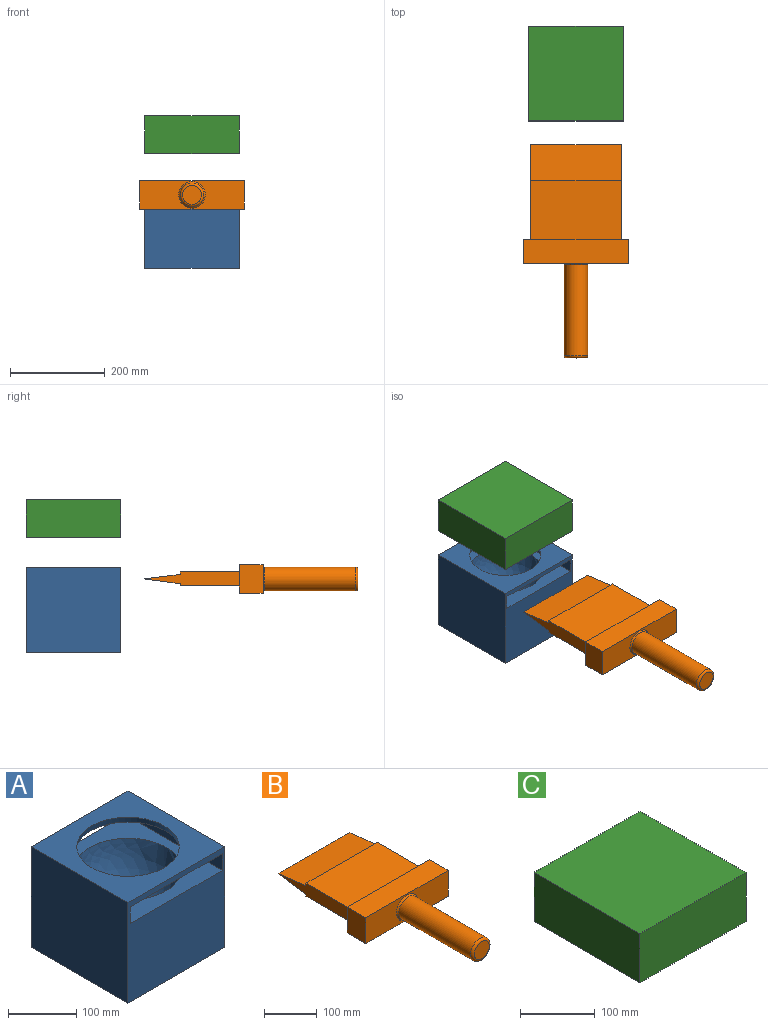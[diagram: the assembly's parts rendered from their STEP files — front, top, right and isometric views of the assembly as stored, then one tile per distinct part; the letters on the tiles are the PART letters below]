
ASSEMBLY  parts=3 mates=2
PART A: 12 faces, bbox 200x200x180 mm
  f0: revolved ~154.02x154.02mm, area 4876.3mm2, adj f2,f9
  f1: plane 200x180mm, normal (1,0,0), area 36000mm2, adj f2,f4,f5,f6
  f2: plane 200.01x200.01mm, normal (0,0,1), area 22330.5mm2, adj f0,f1,f3,f5,f6
  f3: plane 200x180mm, normal (-1,0,0), area 36000mm2, adj f2,f4,f5,f6
  f4: plane 200x200mm, normal (0,0,-1), area 40000mm2, adj f1,f3,f5,f6
  f5: plane 200x180mm, normal (0,-1,0), area 30300mm2, adj f1,f2,f3,f4,f7,f8,f9,f10
  f6: plane 200x180mm, normal (0,1,0), area 30300mm2, adj f1,f2,f3,f4,f7,f8,f9,f10
  f7: plane 200x30mm, normal (1,0,0), area 6000mm2, adj f5,f6,f9,f10
  f8: plane 200x30mm, normal (-1,0,0), area 6000mm2, adj f5,f6,f9,f10
  f9: plane 200x190mm, normal (0,0,-1), area 19369.6mm2, adj f0,f5,f6,f7,f8
  f10: plane 200x190mm, normal (0,0,1), area 18737.3mm2, adj f5,f6,f7,f8,f11
  f11: revolved ~156.61x156.61mm, area 44038.9mm2, adj f10
PART B: 18 faces, bbox 220x449.9x60 mm
  f0: plane 190x4.56mm, normal (0,1,0), area 867.3mm2, adj f1,f3,f4,f16
  f1: plane 199.87x30mm, normal (1,0,0), area 4496.8mm2, adj f0,f2,f4,f5,f11,f16,f17
  f2: plane 190x125mm, normal (0,0,1), area 23750mm2, adj f1,f3,f5,f11
  f3: plane 199.87x30mm, normal (-1,0,0), area 4496.8mm2, adj f0,f2,f4,f5,f11,f16,f17
  f4: plane 190x125mm, normal (0,0,-1), area 23750mm2, adj f0,f1,f3,f11
  f5: plane 190x5.49mm, normal (0,1,0), area 1042.4mm2, adj f1,f2,f3,f17
  f6: plane 60x50mm, normal (1,0,0), area 3000mm2, adj f7,f9,f10,f11
  f7: plane 220x50mm, normal (0,0,1), area 11000mm2, adj f6,f8,f10,f11
  f8: plane 60x50mm, normal (-1,0,0), area 3000mm2, adj f7,f9,f10,f11
  f9: plane 220x50mm, normal (0,0,-1), area 11000mm2, adj f6,f8,f10,f11
  f10: plane 220x60mm, normal (0,-1,0), area 10737mm2, adj f6,f7,f8,f9,f15
  f11: plane 220x60mm, normal (0,1,0), area 7500mm2, adj f1,f2,f3,f4,f6,f7,f8,f9
  f12: cylinder r=25mm len=192mm, axis (0,1,0), area 30159.3mm2, adj f14,f15
  f13: plane 40x40mm, normal (0,-1,0), area 1256.6mm2, adj f14
  f14: torus R=20mm, axis (0,-1,0), area 1144mm2, adj f12,f13
  f15: cone r=25mm half-angle=45deg, axis (0,1,0), area 706.4mm2, adj f10,f12
  f16: plane 190x74.87mm, normal (0,0.14,-0.99), area 14362.6mm2, adj f0,f1,f3,f17
  f17: plane 190x74.87mm, normal (0,0.13,0.99), area 14339.4mm2, adj f1,f3,f5,f16
PART C: 7 faces, bbox 200x200x80 mm
  f0: plane 200x80mm, normal (1,0,0), area 16000mm2, adj f1,f3,f4,f5
  f1: plane 200x200mm, normal (0,0,1), area 40000mm2, adj f0,f2,f4,f5
  f2: plane 200x80mm, normal (-1,0,0), area 16000mm2, adj f1,f3,f4,f5
  f3: plane 200.01x200.01mm, normal (0,0,-1), area 22330.5mm2, adj f0,f2,f4,f5,f6
  f4: plane 200x80mm, normal (0,-1,0), area 16000mm2, adj f0,f1,f2,f3
  f5: plane 200x80mm, normal (0,1,0), area 16000mm2, adj f0,f1,f2,f3
  f6: revolved ~150x150mm, area 23409.5mm2, adj f3
PLACE A t=(1.52,-4.85,-8.62)mm fixed
PLACE B t=(1.52,-292.14,56.38)mm
PLACE C t=(1.52,-4.85,183.51)mm
MATE slider B.f11 <-> A.f5  axis (0,1,0) through (-93.48,-354.64,71.38)mm
MATE slider C.f3 <-> A.f2  axis (0,0,-1) through (1.52,-4.85,143.52)mm
